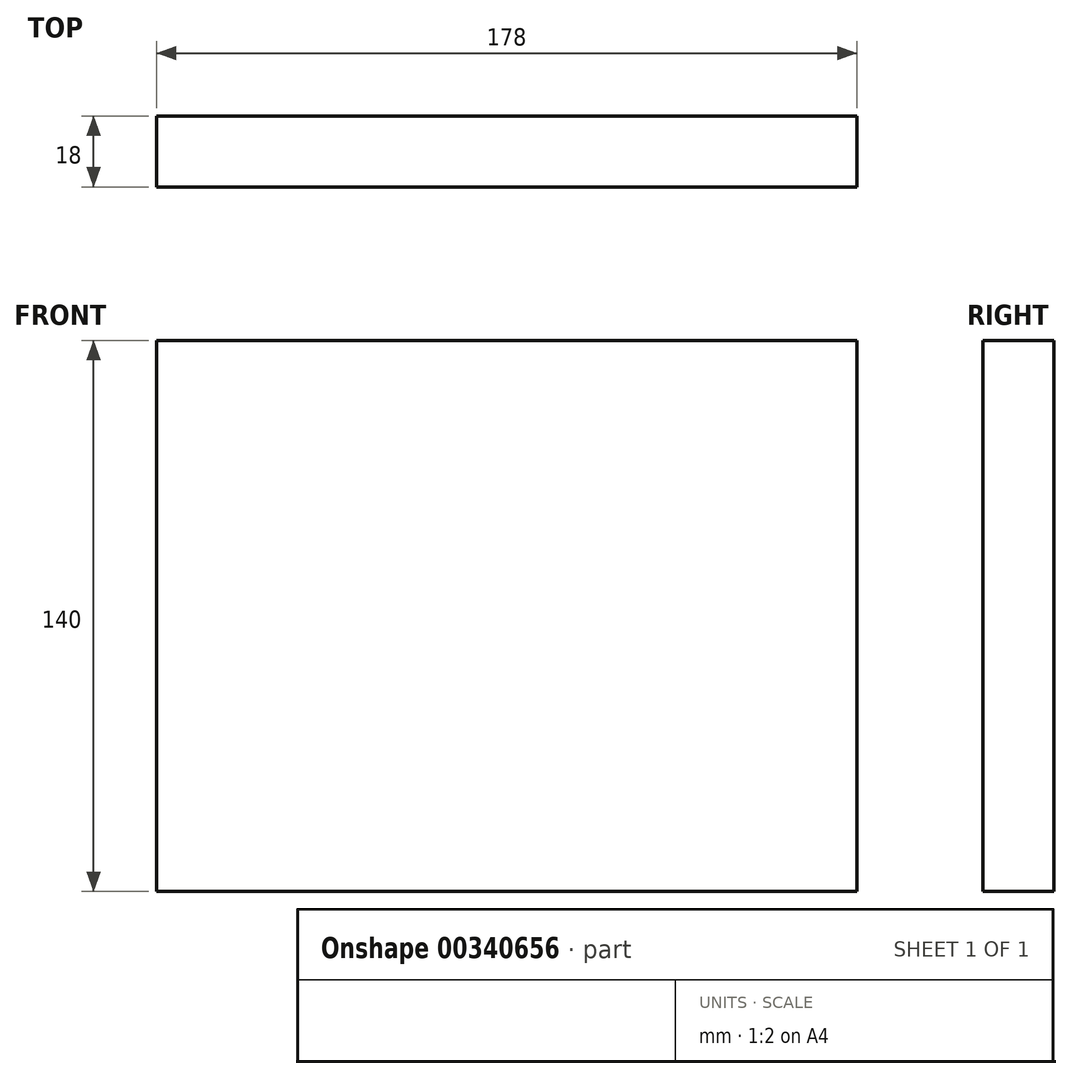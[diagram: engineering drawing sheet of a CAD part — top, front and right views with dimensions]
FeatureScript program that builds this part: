
annotation { "Feature Type Name" : "Feature", "Feature Type Description" : "" }
export const myFeature = defineFeature(function(context is Context, id is Id, definition is map)
    precondition{}
    {
        {
            var Q0;
            Q0=qCreatedBy(makeId("Front.planeOp"),FACE);
            var sketch = newSketch(context, id + "F0", { "sketchPlane" : qUnion([Q0])});
            skLineSegment(sketch, "E0.bottom", {"start": v(-85.05, 98.44) * mm, "end": v(92.95, 98.44) * mm});
            skLineSegment(sketch, "E0.top", {"start": v(-85.05, -41.56) * mm, "end": v(92.95, -41.56) * mm});
            skLineSegment(sketch, "E0.left", {"start": v(-85.05, 98.44) * mm, "end": v(-85.05, -41.56) * mm});
            skLineSegment(sketch, "E0.right", {"start": v(92.95, 98.44) * mm, "end": v(92.95, -41.56) * mm});
            skSolve(sketch);
        }
        {
            var Q0;
            Q0=makeQuery(id+"F0.imprint","IMPRINT",FACE,{"disambiguationData":[TD([[makeQuery(id+"F0.imprint","IMPRINT",EDGE,{"derivedFrom":sQuery(id+"F0.wireOp",EDGE,"E0.bottom")}),-1.0]])]});
            extrude(context, id + "F1", {"entities" : qUnion([Q0]), "oppositeDirection" : true, "depth" : 18 * mm});
        }
    });
